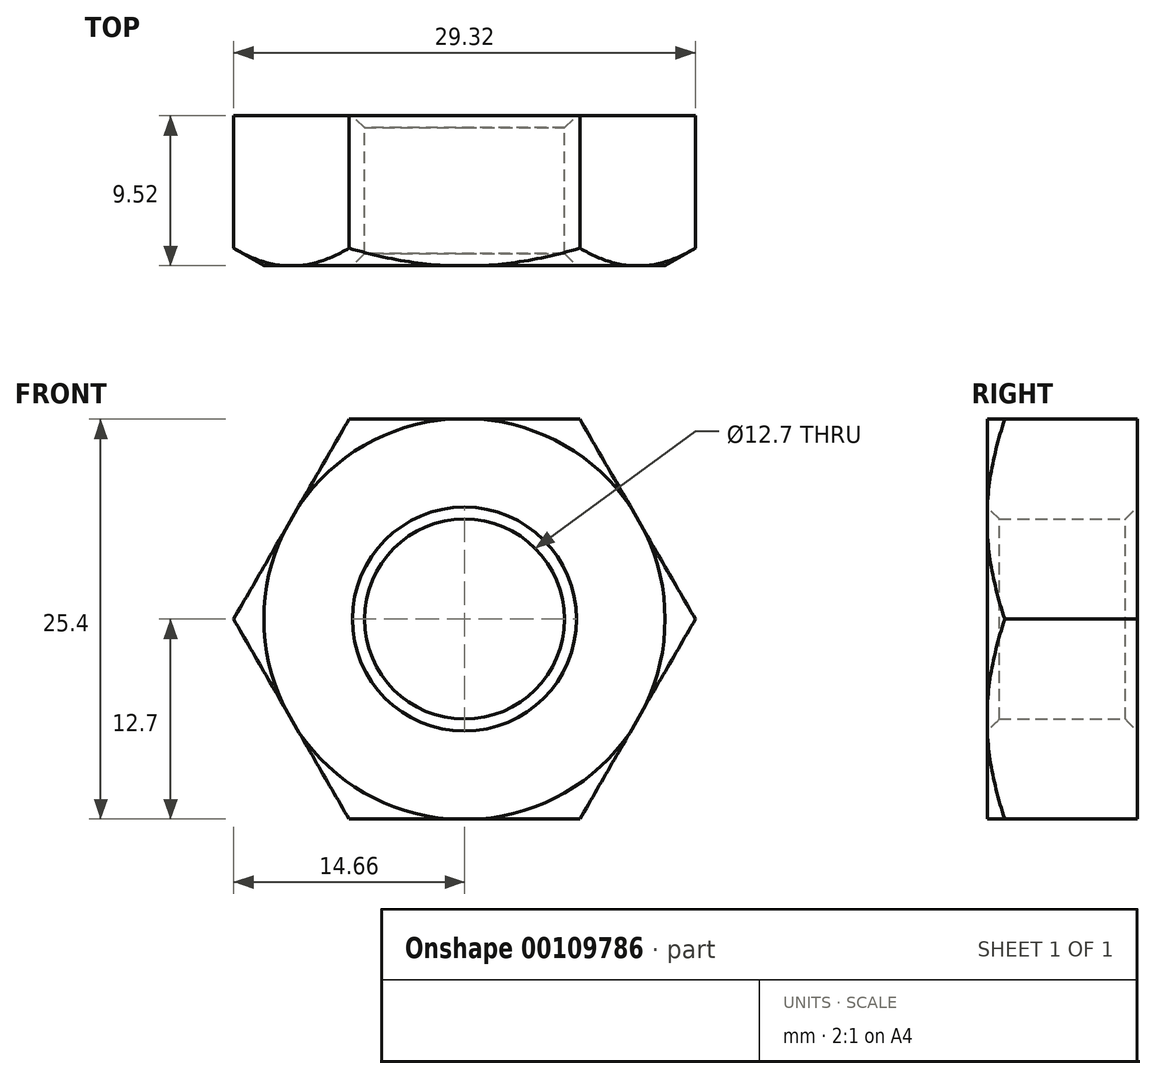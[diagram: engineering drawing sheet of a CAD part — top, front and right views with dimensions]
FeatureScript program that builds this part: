
annotation { "Feature Type Name" : "Feature", "Feature Type Description" : "" }
export const myFeature = defineFeature(function(context is Context, id is Id, definition is map)
    precondition{}
    {
        {
            var Q0;
            Q0=qCreatedBy(makeId("Front.planeOp"),FACE);
            var sketch = newSketch(context, id + "F0", { "sketchPlane" : qUnion([Q0])});
            skCircle(sketch, "E0", {"center": v(0, 0) * mm, "radius": 6.35 * mm});
            skCircle(sketch, "E1.cCircle", {"center": v(0, 0) * mm, "radius": 12.7 * mm, "construction": true});
            skLineSegment(sketch, "E1.0", {"start": v(-7.33, 12.7) * mm, "end": v(7.33, 12.7) * mm});
            skLineSegment(sketch, "E1.1", {"start": v(7.33, 12.7) * mm, "end": v(14.66, 0) * mm});
            skLineSegment(sketch, "E1.2", {"start": v(14.66, 0) * mm, "end": v(7.33, -12.7) * mm});
            skLineSegment(sketch, "E1.3", {"start": v(7.33, -12.7) * mm, "end": v(-7.33, -12.7) * mm});
            skLineSegment(sketch, "E1.4", {"start": v(-7.33, -12.7) * mm, "end": v(-14.66, 0) * mm});
            skLineSegment(sketch, "E1.5", {"start": v(-14.66, 0) * mm, "end": v(-7.33, 12.7) * mm});
            skPoint(sketch, "E1.0.midPoint", {"position": v(0, 12.7) * mm});
            skSolve(sketch);
        }
        {
            var Q0;
            Q0 = qSketchRegion(id + "F0", true);
            extrude(context, id + "F1", {"entities" : qUnion([Q0]), "endBound" : BoundingType.SYMMETRIC, "depth" : 9.52 * mm});
        }
        {
            var Q0;
            Q0=makeQuery(id+"F1.opExtrude","CAP_EDGE",EDGE,{"disambiguationData":[OSD([sQuery(id+"F0.wireOp",EDGE,"E0")])],"isStart":false});
            var Q1;
            Q1=makeQuery(id+"F1.opExtrude","CAP_EDGE",EDGE,{"disambiguationData":[OSD([sQuery(id+"F0.wireOp",EDGE,"E0")])],"isStart":true});
            chamfer(context, id + "F2", {"entities" : qUnion([Q0, Q1]), "width" : 0.76 * mm, "tangentPropagation" : true});
        }
        {
            var Q0;
            Q0=qCreatedBy(makeId("Top.planeOp"),FACE);
            var sketch = newSketch(context, id + "F3", { "sketchPlane" : qUnion([Q0])});
            skLineSegment(sketch, "E2", {"start": v(-12.7, -4.79) * mm, "end": v(-14.84, -3.55) * mm});
            skLineSegment(sketch, "E3", {"start": v(-14.84, -3.55) * mm, "end": v(-14.84, -5.05) * mm});
            skLineSegment(sketch, "E4", {"start": v(-14.84, -5.05) * mm, "end": v(-12.7, -4.79) * mm});
            skSolve(sketch);
        }
        {
            var Q0;
            Q0=makeQuery(id+"F3.imprint","IMPRINT",FACE,{"disambiguationData":[TD([[makeQuery(id+"F3.imprint","IMPRINT",EDGE,{"derivedFrom":sQuery(id+"F3.wireOp",EDGE,"E2")}),1.0]])]});
            var Q1;
            Q1=makeQuery(id+"F3.imprint","IMPRINT",FACE,{"disambiguationData":[TD([[makeQuery(id+"F3.imprint","IMPRINT",EDGE,{"derivedFrom":sQuery(id+"F3.wireOp",EDGE,"c99b1c92-eb93-47db-a1cc-f9a68a046df20.MirrorCS")}),-1.0]])]});
            var Q2;
            {var subQ0=sQuery(id+"F0.wireOp",EDGE,"E0");Q2=makeQuery(id+"F2.opChamfer","BLEND_EDGE",EDGE,{"blendedFrom":[makeQuery(id+"F1.opExtrude","CAP_EDGE",EDGE,{"disambiguationData":[OSD([subQ0])],"isStart":false}),makeQuery(id+"F1.opExtrude","CAP_FACE",FACE,{"disambiguationData":[OSD([subQ0,sQuery(id+"F0.wireOp",EDGE,"E1.0"),sQuery(id+"F0.wireOp",EDGE,"E1.1"),sQuery(id+"F0.wireOp",EDGE,"E1.2"),sQuery(id+"F0.wireOp",EDGE,"E1.3"),sQuery(id+"F0.wireOp",EDGE,"E1.4"),sQuery(id+"F0.wireOp",EDGE,"E1.5")])],"isStart":false})],"blendedInto":[makeQuery(id+"F1.opExtrude","CAP_FACE",FACE,{"disambiguationData":[OSD([subQ0,sQuery(id+"F0.wireOp",EDGE,"E1.0"),sQuery(id+"F0.wireOp",EDGE,"E1.1"),sQuery(id+"F0.wireOp",EDGE,"E1.2"),sQuery(id+"F0.wireOp",EDGE,"E1.3"),sQuery(id+"F0.wireOp",EDGE,"E1.4"),sQuery(id+"F0.wireOp",EDGE,"E1.5")])],"isStart":false})]});}
            sweep(context, id + "F4", {"operationType" : NewBodyOperationType.REMOVE, "profiles" : qUnion([Q0, Q1]), "path" : qUnion([Q2])});
        }
    });
